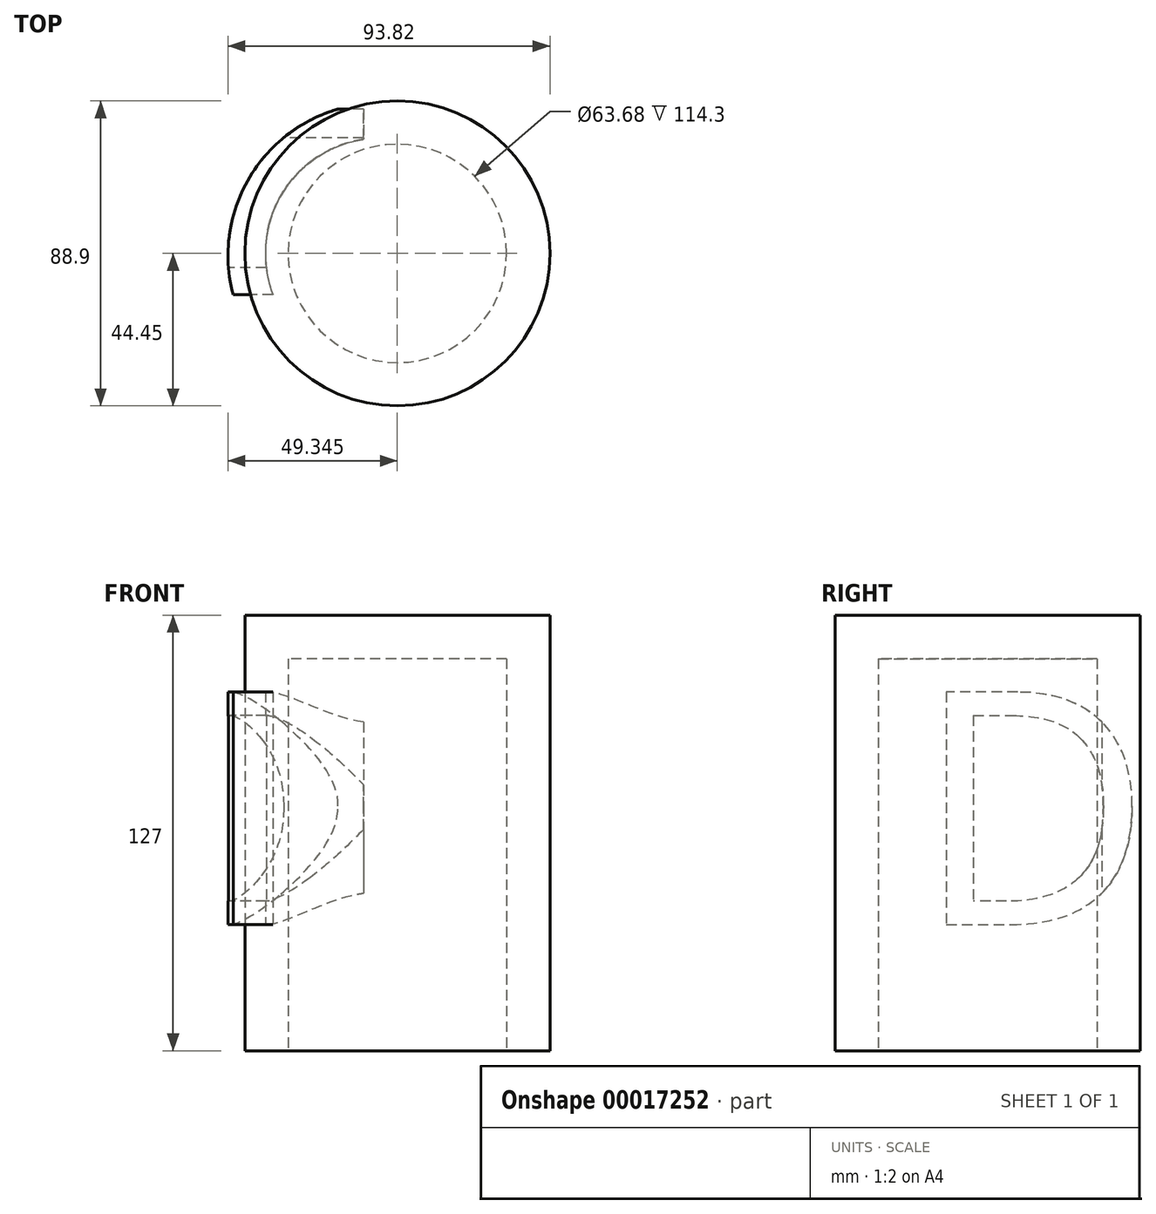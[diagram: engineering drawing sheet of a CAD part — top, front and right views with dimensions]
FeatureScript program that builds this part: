
annotation { "Feature Type Name" : "Feature", "Feature Type Description" : "" }
export const myFeature = defineFeature(function(context is Context, id is Id, definition is map)
    precondition{}
    {
        {
            var Q0;
            Q0=qCreatedBy(makeId("Top.planeOp"),FACE);
            var sketch = newSketch(context, id + "F0", { "sketchPlane" : qUnion([Q0])});
            skCircle(sketch, "E0", {"center": v(38.26, -0.61) * mm, "radius": 44.45 * mm});
            skSolve(sketch);
        }
        {
            var Q0;
            Q0=makeQuery(id+"F0.imprint","IMPRINT",FACE,{"disambiguationData":[TD([[makeQuery(id+"F0.imprint","IMPRINT",EDGE,{"derivedFrom":sQuery(id+"F0.wireOp",EDGE,"E0")}),1.0]])]});
            extrude(context, id + "F1", {"entities" : qUnion([Q0]), "depth" : 127 * mm});
        }
        {
            var Q0;
            Q0=qCreatedBy(makeId("Top.planeOp"),FACE);
            var sketch = newSketch(context, id + "F2", { "sketchPlane" : qUnion([Q0])});
            skCircle(sketch, "E1", {"center": v(38.35, 0) * mm, "radius": 33.66 * mm});
            skSolve(sketch);
        }
        {
            var Q0;
            Q0=makeQuery(id+"F2.imprint","IMPRINT",FACE,{"disambiguationData":[TD([[makeQuery(id+"F2.imprint","IMPRINT",EDGE,{"derivedFrom":sQuery(id+"F2.wireOp",EDGE,"E1")}),1.0]])]});
            extrude(context, id + "F3", {"entities" : qUnion([Q0]), "operationType" : NewBodyOperationType.REMOVE, "depth" : 114.3 * mm});
        }
        {
            var Q0;
            Q0=qCreatedBy(makeId("Right.planeOp"),FACE);
            var sketch = newSketch(context, id + "F4", { "sketchPlane" : qUnion([Q0])});
            skText(sketch, "E2", { "text": "D", "fontName": "OpenSans-Regular.ttf"});
            const initialGuessF4  = {"E2": [-0.02132, 0.03678, 1, 0, 0.06834]};
            skSetInitialGuess(sketch, initialGuessF4);
            skSolve(sketch);
        }
        {
            var Q0;
            Q0=makeQuery(id+"F4.imprint","IMPRINT",FACE,{"disambiguationData":[TD([[makeQuery(id+"F4.imprint","IMPRINT",EDGE,{"derivedFrom":sQuery(id+"F4.wireOp",EDGE,"E2.sketch_text.stroke-0")}),-1.0]])]});
            extrude(context, id + "F5", {"entities" : qUnion([Q0]), "operationType" : NewBodyOperationType.INTERSECT, "depth" : 33.3 * mm, "hasSecondDirection" : true, "secondDirectionOppositeDirection" : true, "secondDirectionDepth" : 25.4 * mm});
        }
        {
            var Q0;
            Q0=qCreatedBy(makeId("Top.planeOp"),FACE);
            var sketch = newSketch(context, id + "F6", { "sketchPlane" : qUnion([Q0])});
            skCircle(sketch, "E3", {"center": v(43.18, 0) * mm, "radius": 44.45 * mm});
            skSolve(sketch);
        }
        {
            var Q0;
            Q0=makeQuery(id+"F6.imprint","IMPRINT",FACE,{"disambiguationData":[TD([[makeQuery(id+"F6.imprint","IMPRINT",EDGE,{"derivedFrom":sQuery(id+"F6.wireOp",EDGE,"E3")}),1.0]])]});
            extrude(context, id + "F7", {"entities" : qUnion([Q0]), "depth" : 127 * mm});
        }
        {
            var Q0;
            Q0=qCreatedBy(makeId("Top.planeOp"),FACE);
            var sketch = newSketch(context, id + "F8", { "sketchPlane" : qUnion([Q0])});
            skCircle(sketch, "E4", {"center": v(43.16, 0) * mm, "radius": 31.84 * mm});
            skSolve(sketch);
        }
        {
            var Q0;
            Q0=makeQuery(id+"F8.imprint","IMPRINT",FACE,{"disambiguationData":[TD([[makeQuery(id+"F8.imprint","IMPRINT",EDGE,{"derivedFrom":sQuery(id+"F8.wireOp",EDGE,"E4")}),1.0]])]});
            extrude(context, id + "F9", {"entities" : qUnion([Q0]), "operationType" : NewBodyOperationType.REMOVE, "depth" : 114.3 * mm});
        }
    });
